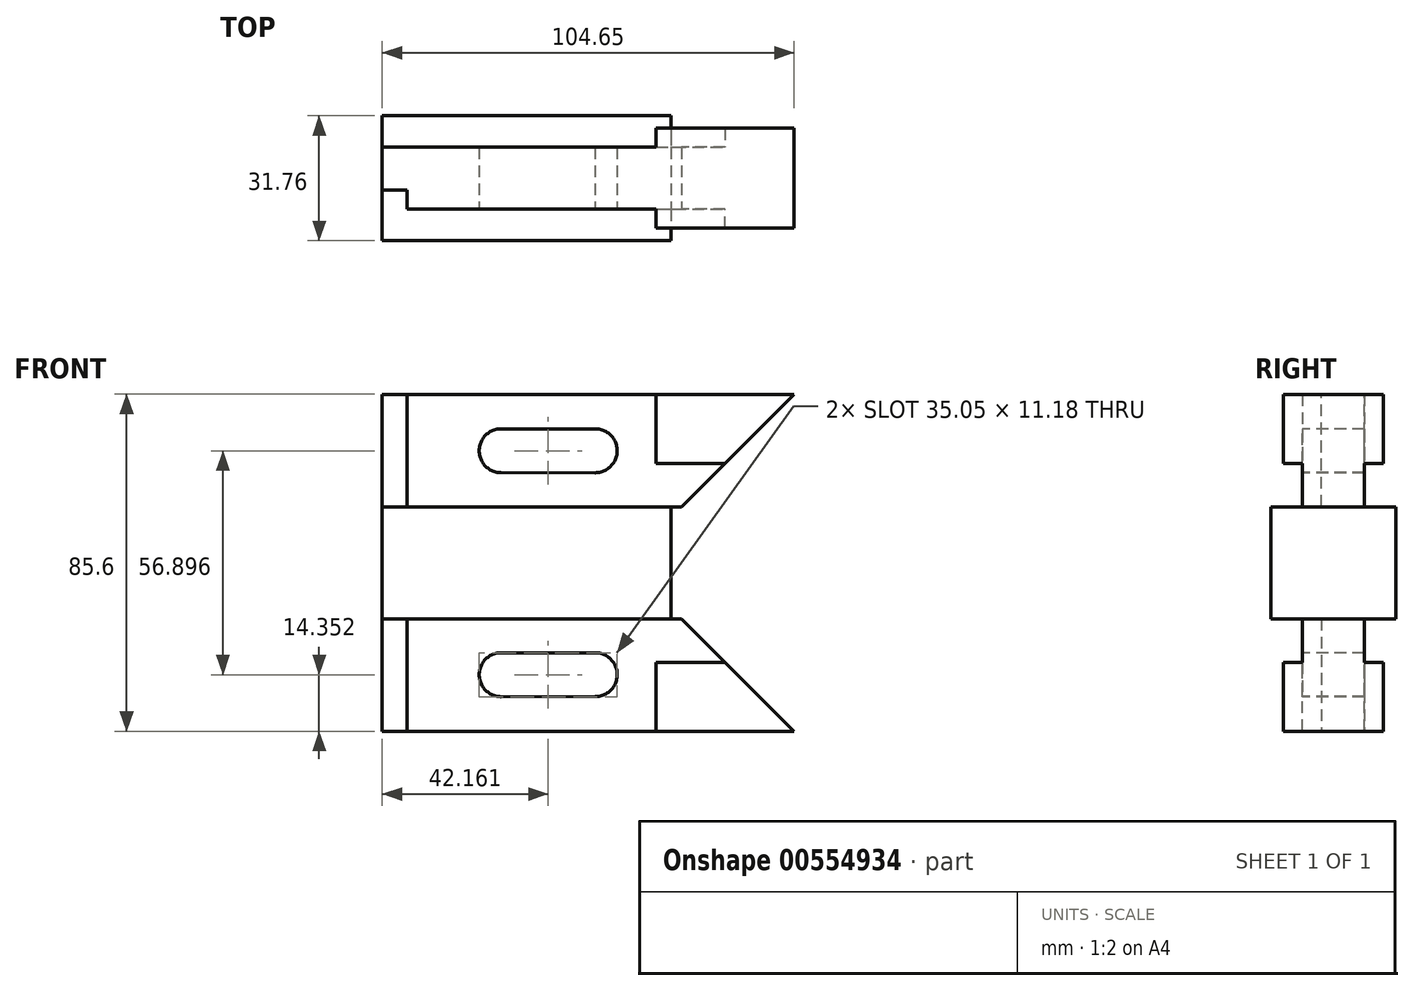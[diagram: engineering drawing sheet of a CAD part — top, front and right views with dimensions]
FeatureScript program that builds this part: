
annotation { "Feature Type Name" : "Feature", "Feature Type Description" : "" }
export const myFeature = defineFeature(function(context is Context, id is Id, definition is map)
    precondition{}
    {
        {
            var Q0;
            Q0=qCreatedBy(makeId("Top.planeOp"),FACE);
            var sketch = newSketch(context, id + "F0", { "sketchPlane" : qUnion([Q0])});
            skLineSegment(sketch, "E0.bottom", {"start": v(-36.7, 15.87) * mm, "end": v(36.7, 15.87) * mm});
            skLineSegment(sketch, "E0.top", {"start": v(-36.7, -15.88) * mm, "end": v(36.7, -15.88) * mm});
            skLineSegment(sketch, "E0.left", {"start": v(-36.7, 15.87) * mm, "end": v(-36.7, -15.87) * mm});
            skLineSegment(sketch, "E0.right", {"start": v(36.7, 15.87) * mm, "end": v(36.7, -15.87) * mm});
            skPoint(sketch, "E0.middle", {"position": v(0, 0) * mm});
            skSolve(sketch);
        }
        {
            var Q0;
            Q0=makeQuery(id+"F0.imprint","IMPRINT",FACE,{"disambiguationData":[TD([[makeQuery(id+"F0.imprint","IMPRINT",EDGE,{"derivedFrom":sQuery(id+"F0.wireOp",EDGE,"E0.bottom")}),-1.0]])]});
            extrude(context, id + "F1", {"entities" : qUnion([Q0]), "depth" : 14.22 * mm, "offsetDistance" : 25.4 * mm});
        }
        {
            var Q0;
            Q0=qCreatedBy(makeId("Front.planeOp"),FACE);
            var sketch = newSketch(context, id + "F2", { "sketchPlane" : qUnion([Q0])});
            skLineSegment(sketch, "E1", {"start": v(-36.7, 14.22) * mm, "end": v(-36.7, 42.8) * mm});
            skLineSegment(sketch, "E2", {"start": v(-36.7, 42.8) * mm, "end": v(67.95, 42.8) * mm});
            skLineSegment(sketch, "E3", {"start": v(-36.7, 14.22) * mm, "end": v(39.37, 14.22) * mm});
            skLineSegment(sketch, "E4", {"start": v(-36.7, 42.8) * mm, "end": v(-30.35, 42.8) * mm});
            skLineSegment(sketch, "E5", {"start": v(-30.35, 42.8) * mm, "end": v(-30.35, 14.22) * mm});
            skLineSegment(sketch, "E6", {"start": v(-36.7, 42.8) * mm, "end": v(32.9, 42.8) * mm});
            skLineSegment(sketch, "E7", {"start": v(32.9, 42.8) * mm, "end": v(32.9, 25.17) * mm});
            skLineSegment(sketch, "E8", {"start": v(32.9, 25.17) * mm, "end": v(50.32, 25.17) * mm});
            skLineSegment(sketch, "E9", {"start": v(67.94, 42.8) * mm, "end": v(39.37, 14.22) * mm});
            skArc(sketch, "E10", {"start": v(-6.48, 34.04) * mm, "mid": v(-12.06, 28.45) * mm, "end": v(-6.48, 22.86) * mm});
            skArc(sketch, "E11", {"start": v(17.4, 22.86) * mm, "mid": v(22.99, 28.5) * mm, "end": v(17.31, 34.04) * mm});
            skLineSegment(sketch, "E12", {"start": v(-6.48, 22.86) * mm, "end": v(17.4, 22.86) * mm});
            skLineSegment(sketch, "E13", {"start": v(17.49, 34.04) * mm, "end": v(-6.48, 34.04) * mm});
            skLineSegment(sketch, "E14", {"start": v(-12.07, 28.45) * mm, "end": v(22.99, 28.45) * mm, "construction": true});
            skSolve(sketch);
        }
        {
            var Q0;
            {var subQ10=sQuery(id+"F2.wireOp",EDGE,"E5");Q0=makeQuery(id+"F2.imprint","IMPRINT",FACE,{"disambiguationData":[TD([[makeQuery(id+"F2.imprint","IMPRINT",EDGE,{"derivedFrom":subQ10}),1.0]])]});}
            var Q1;
            {var subQ0=sQuery(id+"F2.wireOp",EDGE,"E2");Q1=makeQuery(id+"F2.imprint","IMPRINT",FACE,{"disambiguationData":[TD([[makeQuery(id+"F2.imprint","IMPRINT",EDGE,{"derivedFrom":subQ0}),-1.0]])]});}
            var Q2;
            {var subQ0=sQuery(id+"F2.wireOp",EDGE,"E1");Q2=makeQuery(id+"F2.imprint","IMPRINT",FACE,{"disambiguationData":[TD([[makeQuery(id+"F2.imprint","IMPRINT",EDGE,{"derivedFrom":subQ0}),-1.0]])]});}
            extrude(context, id + "F3", {"entities" : qUnion([Q0, Q1, Q2]), "operationType" : NewBodyOperationType.ADD, "oppositeDirection" : true, "depth" : 7.87 * mm, "offsetDistance" : 25.4 * mm});
        }
        {
            var Q0;
            Q0=makeQuery(id+"F3.opExtrude","CAP_FACE",FACE,{"disambiguationData":[OSD([sQuery(id+"F2.wireOp",EDGE,"E1"),sQuery(id+"F2.wireOp",EDGE,"E2"),sQuery(id+"F2.wireOp",EDGE,"E3"),sQuery(id+"F2.wireOp",EDGE,"E6"),sQuery(id+"F2.wireOp",EDGE,"E9"),sQuery(id+"F2.wireOp",EDGE,"E10"),sQuery(id+"F2.wireOp",EDGE,"E11"),sQuery(id+"F2.wireOp",EDGE,"E12"),sQuery(id+"F2.wireOp",EDGE,"E13")])],"isStart":true});
            var sketch = newSketch(context, id + "F4", { "sketchPlane" : qUnion([Q0])});
            skLineSegment(sketch, "E15", {"start": v(-36.7, 42.8) * mm, "end": v(-30.35, 42.8) * mm});
            skLineSegment(sketch, "E16", {"start": v(-30.35, 42.8) * mm, "end": v(-30.35, 14.22) * mm});
            skSolve(sketch);
        }
        {
            var Q0;
            Q0 = qSketchRegion(id + "F4", true);
            var Q1;
            {var subQ6=sQuery(id+"F4.wireOp",EDGE,"E16");Q1=makeQuery(id+"F4.imprint","IMPRINT",FACE,{"disambiguationData":[TD([[makeQuery(id+"F4.imprint","IMPRINT",EDGE,{"derivedFrom":subQ6}),1.0]])]});}
            extrude(context, id + "F5", {"entities" : qUnion([Q0, Q1]), "operationType" : NewBodyOperationType.ADD, "depth" : 7.87 * mm, "offsetDistance" : 25.4 * mm});
        }
        {
            var Q0;
            Q0=makeQuery(id+"F3.opExtrude","CAP_FACE",FACE,{"disambiguationData":[OSD([sQuery(id+"F2.wireOp",EDGE,"E1"),sQuery(id+"F2.wireOp",EDGE,"E2"),sQuery(id+"F2.wireOp",EDGE,"E3"),sQuery(id+"F2.wireOp",EDGE,"E6"),sQuery(id+"F2.wireOp",EDGE,"E9"),sQuery(id+"F2.wireOp",EDGE,"E10"),sQuery(id+"F2.wireOp",EDGE,"E11"),sQuery(id+"F2.wireOp",EDGE,"E12"),sQuery(id+"F2.wireOp",EDGE,"E13")])],"isStart":true});
            extrude(context, id + "F6", {"entities" : qUnion([Q0]), "operationType" : NewBodyOperationType.ADD, "depth" : 3.05 * mm, "offsetDistance" : 25.4 * mm});
        }
        {
            var Q0;
            Q0=makeQuery(id+"F5.opExtrude","CAP_FACE",FACE,{"disambiguationData":[OSD([sQuery(id+"F2.wireOp",EDGE,"E2"),sQuery(id+"F2.wireOp",EDGE,"E3"),sQuery(id+"F2.wireOp",EDGE,"E6"),sQuery(id+"F2.wireOp",EDGE,"E9"),sQuery(id+"F2.wireOp",EDGE,"E10"),sQuery(id+"F2.wireOp",EDGE,"E11"),sQuery(id+"F2.wireOp",EDGE,"E12"),sQuery(id+"F2.wireOp",EDGE,"E13"),sQuery(id+"F4.wireOp",EDGE,"E16")])],"isStart":false});
            var sketch = newSketch(context, id + "F7", { "sketchPlane" : qUnion([Q0])});
            skLineSegment(sketch, "E17", {"start": v(67.95, 42.8) * mm, "end": v(32.9, 42.8) * mm});
            skLineSegment(sketch, "E18", {"start": v(32.9, 42.8) * mm, "end": v(32.9, 25.27) * mm});
            skLineSegment(sketch, "E19", {"start": v(32.9, 25.27) * mm, "end": v(50.42, 25.27) * mm});
            skSolve(sketch);
        }
        {
            var Q0;
            {var subQ0=sQuery(id+"F7.wireOp",EDGE,"E17");Q0=makeQuery(id+"F7.imprint","IMPRINT",FACE,{"disambiguationData":[TD([[makeQuery(id+"F7.imprint","IMPRINT",EDGE,{"derivedFrom":subQ0}),-1.0]])]});}
            extrude(context, id + "F8", {"entities" : qUnion([Q0]), "operationType" : NewBodyOperationType.ADD, "depth" : 4.83 * mm, "offsetDistance" : 25.4 * mm});
        }
        {
            var Q0;
            Q0=makeQuery(id+"F3.opExtrude","CAP_FACE",FACE,{"disambiguationData":[OSD([sQuery(id+"F2.wireOp",EDGE,"E1"),sQuery(id+"F2.wireOp",EDGE,"E2"),sQuery(id+"F2.wireOp",EDGE,"E3"),sQuery(id+"F2.wireOp",EDGE,"E6"),sQuery(id+"F2.wireOp",EDGE,"E9"),sQuery(id+"F2.wireOp",EDGE,"E10"),sQuery(id+"F2.wireOp",EDGE,"E11"),sQuery(id+"F2.wireOp",EDGE,"E12"),sQuery(id+"F2.wireOp",EDGE,"E13")])],"isStart":false});
            var sketch = newSketch(context, id + "F9", { "sketchPlane" : qUnion([Q0])});
            skLineSegment(sketch, "E20", {"start": v(-67.95, 42.8) * mm, "end": v(-32.9, 42.8) * mm});
            skLineSegment(sketch, "E21", {"start": v(-32.9, 42.8) * mm, "end": v(-32.9, 25.27) * mm});
            skLineSegment(sketch, "E22", {"start": v(-32.9, 25.27) * mm, "end": v(-50.42, 25.27) * mm});
            skSolve(sketch);
        }
        {
            var Q0;
            Q0 = qSketchRegion(id + "F9", true);
            var Q1;
            {var subQ0=sQuery(id+"F9.wireOp",EDGE,"E20");Q1=makeQuery(id+"F9.imprint","IMPRINT",FACE,{"disambiguationData":[TD([[makeQuery(id+"F9.imprint","IMPRINT",EDGE,{"derivedFrom":subQ0}),1.0]])]});}
            extrude(context, id + "F10", {"entities" : qUnion([Q0, Q1]), "operationType" : NewBodyOperationType.ADD, "depth" : 4.83 * mm, "offsetDistance" : 25.4 * mm});
        }
        {
            var Q0;
            Q0=makeQuery(id+"F1.opExtrude","SWEPT_BODY",BODY,{"disambiguationData":[OSD([sQuery(id+"F0.wireOp",EDGE,"E0.bottom"),sQuery(id+"F0.wireOp",EDGE,"E0.top"),sQuery(id+"F0.wireOp",EDGE,"E0.left"),sQuery(id+"F0.wireOp",EDGE,"E0.right")])]});
            var Q1;
            Q1=qCreatedBy(makeId("Top.planeOp"),FACE);
            mirror(context, id + "F11", {"operationType" : NewBodyOperationType.ADD, "entities" : qUnion([Q0]), "mirrorPlane" : qUnion([Q1])});
        }
    });
